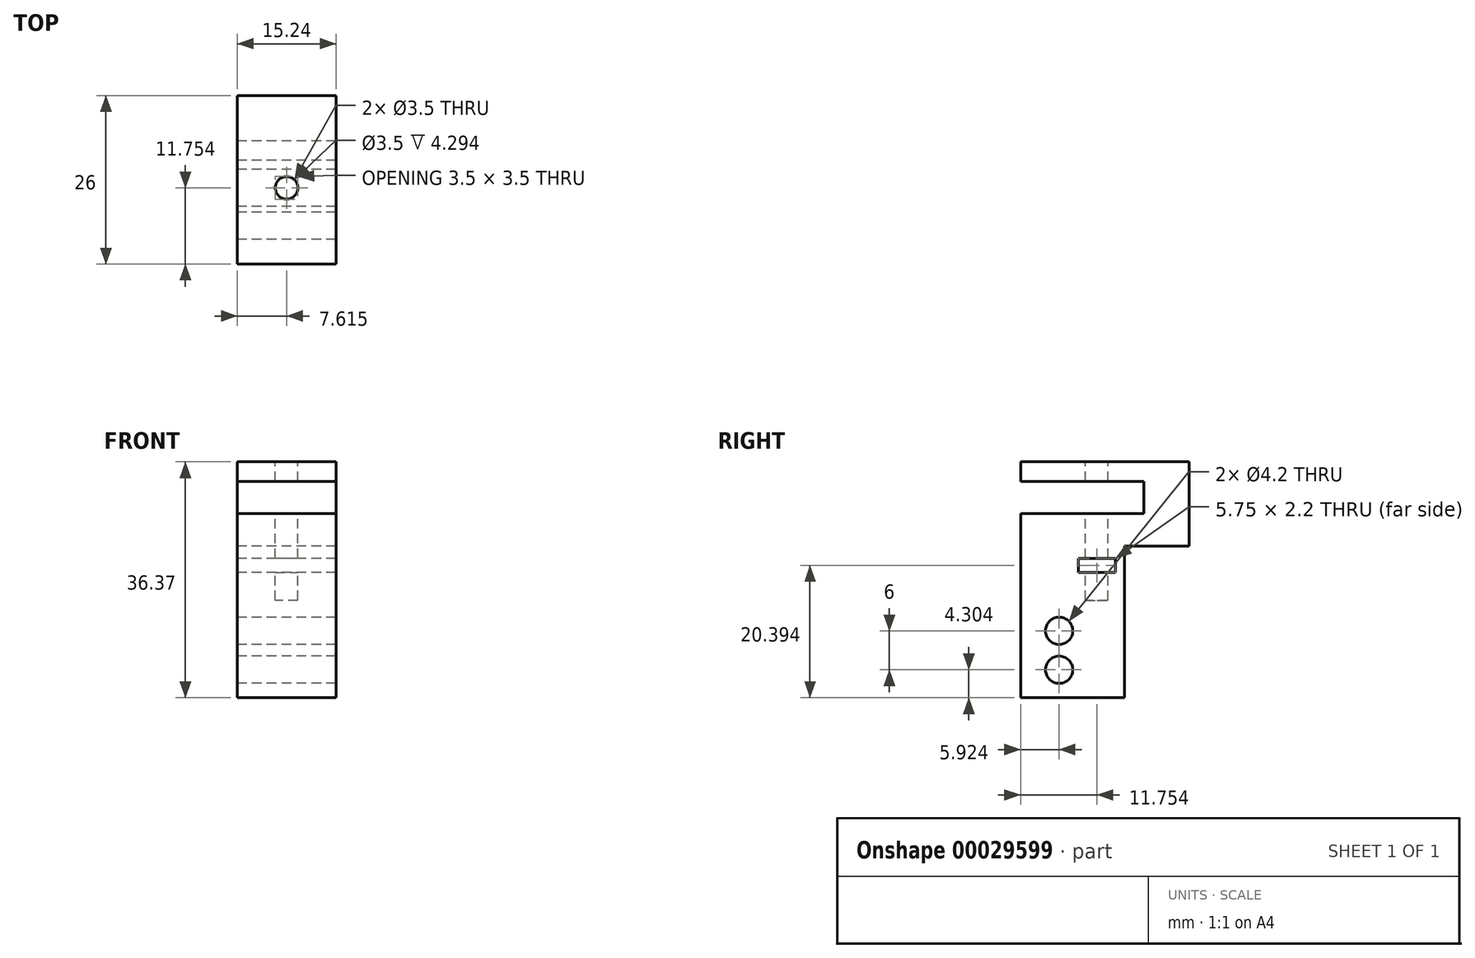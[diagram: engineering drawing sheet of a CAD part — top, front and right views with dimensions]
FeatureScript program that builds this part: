
annotation { "Feature Type Name" : "Feature", "Feature Type Description" : "" }
export const myFeature = defineFeature(function(context is Context, id is Id, definition is map)
    precondition{}
    {
        {
            var Q0;
            Q0=qCreatedBy(makeId("Top.planeOp"),FACE);
            var sketch = newSketch(context, id + "F0", { "sketchPlane" : qUnion([Q0])});
            skLineSegment(sketch, "E0.bottom", {"start": v(-10.08, 8.84) * mm, "end": v(5.16, 8.84) * mm});
            skLineSegment(sketch, "E0.top", {"start": v(-10.08, -9.16) * mm, "end": v(5.16, -9.16) * mm});
            skLineSegment(sketch, "E0.left", {"start": v(-10.08, 8.84) * mm, "end": v(-10.08, -9.16) * mm});
            skLineSegment(sketch, "E0.right", {"start": v(5.16, 8.84) * mm, "end": v(5.16, -9.16) * mm});
            skSolve(sketch);
        }
        {
            var Q0;
            Q0 = qSketchRegion(id + "F0", true);
            extrude(context, id + "F1", {"entities" : qUnion([Q0]), "depth" : 40 * mm});
        }
        {
            var Q0;
            Q0=makeQuery(id+"F1.opExtrude","SWEPT_FACE",FACE,{"disambiguationData":[OSD([sQuery(id+"F0.wireOp",EDGE,"E0.left")])]});
            var sketch = newSketch(context, id + "F2", { "sketchPlane" : qUnion([Q0])});
            skLineSegment(sketch, "E1.0", {"start": v(-8.84, 40) * mm, "end": v(9.16, 40) * mm, "construction": true});
            skLineSegment(sketch, "E2.0", {"start": v(9.16, 40) * mm, "end": v(9.16, 0) * mm, "construction": true});
            skLineSegment(sketch, "E3.0", {"start": v(-8.84, 40) * mm, "end": v(-8.84, 0) * mm, "construction": true});
            skLineSegment(sketch, "E4.0", {"start": v(-8.84, 0) * mm, "end": v(9.16, 0) * mm, "construction": true});
            skCircle(sketch, "E5", {"center": v(3.24, 10.3) * mm, "radius": 2.1 * mm});
            skLineSegment(sketch, "E6", {"start": v(3.24, 10.3) * mm, "end": v(3.24, -1.7) * mm, "construction": true});
            skCircle(sketch, "E7", {"center": v(3.24, 4.3) * mm, "radius": 2.1 * mm});
            skSolve(sketch);
        }
        {
            var Q0;
            Q0 = qSketchRegion(id + "F2", true);
            var Q1;
            Q1=makeQuery(id+"F1.opExtrude","SWEPT_FACE",FACE,{"disambiguationData":[OSD([sQuery(id+"F0.wireOp",EDGE,"E0.right")])]});
            extrude(context, id + "F3", {"entities" : qUnion([Q0]), "operationType" : NewBodyOperationType.REMOVE, "endBound" : BoundingType.UP_TO_SURFACE, "oppositeDirection" : true, "endBoundEntityFace" : qUnion([Q1]), "depth" : 25 * mm});
        }
        {
            var Q0;
            Q0=makeQuery(id+"F1.opExtrude","CAP_FACE",FACE,{"disambiguationData":[OSD([sQuery(id+"F0.wireOp",EDGE,"E0.bottom"),sQuery(id+"F0.wireOp",EDGE,"E0.top"),sQuery(id+"F0.wireOp",EDGE,"E0.left"),sQuery(id+"F0.wireOp",EDGE,"E0.right")])],"isStart":false});
            var sketch = newSketch(context, id + "F4", { "sketchPlane" : qUnion([Q0])});
            skLineSegment(sketch, "E8.0", {"start": v(-10.08, 8.84) * mm, "end": v(5.16, 8.84) * mm, "construction": true});
            skLineSegment(sketch, "E9", {"start": v(-2.46, 8.84) * mm, "end": v(-2.46, -17.2) * mm, "construction": true});
            skCircle(sketch, "E10", {"center": v(-2.46, 2.6) * mm, "radius": 1.75 * mm});
            skSolve(sketch);
        }
        {
            var Q0;
            Q0=makeQuery(id+"F4.imprint","IMPRINT",FACE,{"disambiguationData":[TD([[makeQuery(id+"F4.imprint","IMPRINT",EDGE,{"derivedFrom":sQuery(id+"F4.wireOp",EDGE,"E10")}),1.0]])]});
            extrude(context, id + "F5", {"entities" : qUnion([Q0]), "operationType" : NewBodyOperationType.REMOVE, "oppositeDirection" : true, "depth" : 25 * mm});
        }
        {
            var Q0;
            Q0=makeQuery(id+"F1.opExtrude","SWEPT_FACE",FACE,{"disambiguationData":[OSD([sQuery(id+"F0.wireOp",EDGE,"E0.left")])]});
            var sketch = newSketch(context, id + "F6", { "sketchPlane" : qUnion([Q0])});
            skLineSegment(sketch, "E11.0", {"start": v(-4.34, 25.3) * mm, "end": v(-0.84, 25.3) * mm, "construction": true});
            skLineSegment(sketch, "E12", {"start": v(-2.6, 25.3) * mm, "end": v(-2.6, 5.75) * mm, "construction": true});
            skLineSegment(sketch, "E13.bottom", {"start": v(-5.47, 21.5) * mm, "end": v(0.28, 21.5) * mm});
            skLineSegment(sketch, "E13.top", {"start": v(-5.47, 19.3) * mm, "end": v(0.28, 19.3) * mm});
            skLineSegment(sketch, "E13.left", {"start": v(-5.47, 21.5) * mm, "end": v(-5.47, 19.3) * mm});
            skLineSegment(sketch, "E13.right", {"start": v(0.28, 21.5) * mm, "end": v(0.28, 19.3) * mm});
            skLineSegment(sketch, "E14.0", {"start": v(-8.84, 40) * mm, "end": v(-8.84, 0) * mm, "construction": true});
            skSolve(sketch);
        }
        {
            var Q0;
            Q0 = qSketchRegion(id + "F6", true);
            var Q1;
            Q1=makeQuery(id+"F1.opExtrude","SWEPT_FACE",FACE,{"disambiguationData":[OSD([sQuery(id+"F0.wireOp",EDGE,"E0.right")])]});
            extrude(context, id + "F7", {"entities" : qUnion([Q0]), "operationType" : NewBodyOperationType.REMOVE, "endBound" : BoundingType.UP_TO_SURFACE, "oppositeDirection" : true, "endBoundEntityFace" : qUnion([Q1]), "depth" : 25 * mm});
        }
        {
            var Q0;
            Q0=makeQuery(id+"F1.opExtrude","SWEPT_FACE",FACE,{"disambiguationData":[OSD([sQuery(id+"F0.wireOp",EDGE,"E0.left")])]});
            var sketch = newSketch(context, id + "F8", { "sketchPlane" : qUnion([Q0])});
            skLineSegment(sketch, "E15.0", {"start": v(-5.47, 21.5) * mm, "end": v(0.28, 21.5) * mm, "construction": true});
            skPoint(sketch, "E16.orphan", {"position": v(-8.84, 0) * mm});
            skLineSegment(sketch, "E17.0", {"start": v(-8.84, 40) * mm, "end": v(-8.84, 23.37) * mm});
            skLineSegment(sketch, "E18", {"start": v(-8.84, 40) * mm, "end": v(-18.84, 40) * mm});
            skLineSegment(sketch, "E19", {"start": v(-18.84, 40) * mm, "end": v(-18.84, 23.37) * mm});
            skLineSegment(sketch, "E20", {"start": v(-18.84, 23.37) * mm, "end": v(-8.84, 23.37) * mm});
            skSolve(sketch);
        }
        {
            var Q0;
            Q0 = qSketchRegion(id + "F8", true);
            var Q1;
            Q1=makeQuery(id+"F1.opExtrude","SWEPT_FACE",FACE,{"disambiguationData":[OSD([sQuery(id+"F0.wireOp",EDGE,"E0.right")])]});
            extrude(context, id + "F9", {"entities" : qUnion([Q0]), "endBound" : BoundingType.UP_TO_SURFACE, "oppositeDirection" : true, "endBoundEntityFace" : qUnion([Q1]), "depth" : 18 * mm});
        }
        {
            var Q0;
            Q0=makeQuery(id+"F1.opExtrude","SWEPT_BODY",BODY,{"disambiguationData":[OSD([sQuery(id+"F0.wireOp",EDGE,"E0.bottom"),sQuery(id+"F0.wireOp",EDGE,"E0.top"),sQuery(id+"F0.wireOp",EDGE,"E0.left"),sQuery(id+"F0.wireOp",EDGE,"E0.right")])]});
            var Q1;
            Q1=makeQuery(id+"F9.opExtrude","SWEPT_BODY",BODY,{"disambiguationData":[OSD([sQuery(id+"F8.wireOp",EDGE,"E17.0"),sQuery(id+"F8.wireOp",EDGE,"E18"),sQuery(id+"F8.wireOp",EDGE,"E19"),sQuery(id+"F8.wireOp",EDGE,"E20")])]});
            booleanBodies(context, id + "F10", {"operationType" : BooleanOperationType.UNION, "tools" : qUnion([Q0, Q1])});
        }
        {
            var Q0;
            Q0=makeQuery(id+"F1.opExtrude","SWEPT_FACE",FACE,{"disambiguationData":[OSD([sQuery(id+"F0.wireOp",EDGE,"E0.left")])]});
            var sketch = newSketch(context, id + "F11", { "sketchPlane" : qUnion([Q0])});
            skLineSegment(sketch, "E21.0", {"start": v(9.16, 40) * mm, "end": v(9.16, 0) * mm});
            skLineSegment(sketch, "E22", {"start": v(9.16, 28.37) * mm, "end": v(-9.84, 28.37) * mm});
            skLineSegment(sketch, "E23", {"start": v(-9.84, 28.37) * mm, "end": v(-9.84, 33.37) * mm});
            skLineSegment(sketch, "E24", {"start": v(-9.84, 33.37) * mm, "end": v(9.16, 33.37) * mm});
            skSolve(sketch);
        }
        {
            var Q0;
            Q0 = qSketchRegion(id + "F11", true);
            extrude(context, id + "F12", {"entities" : qUnion([Q0]), "operationType" : NewBodyOperationType.REMOVE, "oppositeDirection" : true, "depth" : 25 * mm});
        }
        {
            var Q0;
            Q0=makeQuery(id+"F10.opBoolean","MERGE",FACE,{"derivedFrom":[makeQuery(id+"F1.opExtrude","SWEPT_FACE",FACE,{"disambiguationData":[OSD([sQuery(id+"F0.wireOp",EDGE,"E0.left")])]}),makeQuery(id+"F9.opExtrude","CAP_FACE",FACE,{"disambiguationData":[OSD([sQuery(id+"F8.wireOp",EDGE,"E17.0"),sQuery(id+"F8.wireOp",EDGE,"E18"),sQuery(id+"F8.wireOp",EDGE,"E19"),sQuery(id+"F8.wireOp",EDGE,"E20")])],"isStart":true})]});
            var sketch = newSketch(context, id + "F13", { "sketchPlane" : qUnion([Q0])});
            skLineSegment(sketch, "E25.0.2", {"start": v(-9.84, 33.37) * mm, "end": v(9.16, 33.37) * mm, "construction": true});
            skLineSegment(sketch, "E26", {"start": v(-18.84, 43.06) * mm, "end": v(9.16, 43.06) * mm});
            skLineSegment(sketch, "E27", {"start": v(-18.84, 36.37) * mm, "end": v(9.16, 36.37) * mm});
            skLineSegment(sketch, "E28", {"start": v(-18.84, 43.06) * mm, "end": v(-18.84, 36.37) * mm});
            skLineSegment(sketch, "E29", {"start": v(9.16, 43.06) * mm, "end": v(9.16, 36.37) * mm});
            skSolve(sketch);
        }
        {
            var Q0;
            Q0 = qSketchRegion(id + "F13", true);
            extrude(context, id + "F14", {"entities" : qUnion([Q0]), "operationType" : NewBodyOperationType.REMOVE, "oppositeDirection" : true, "depth" : 25 * mm});
        }
        {
            var Q0;
            Q0=makeQuery(id+"F10.opBoolean","MERGE",FACE,{"derivedFrom":[makeQuery(id+"F1.opExtrude","SWEPT_FACE",FACE,{"disambiguationData":[OSD([sQuery(id+"F0.wireOp",EDGE,"E0.left")])]}),makeQuery(id+"F9.opExtrude","CAP_FACE",FACE,{"disambiguationData":[OSD([sQuery(id+"F8.wireOp",EDGE,"E17.0"),sQuery(id+"F8.wireOp",EDGE,"E18"),sQuery(id+"F8.wireOp",EDGE,"E19"),sQuery(id+"F8.wireOp",EDGE,"E20")])],"isStart":true})]});
            var sketch = newSketch(context, id + "F15", { "sketchPlane" : qUnion([Q0])});
            skLineSegment(sketch, "E30.0", {"start": v(-18.84, 36.37) * mm, "end": v(-18.84, 23.37) * mm});
            skLineSegment(sketch, "E31.0", {"start": v(-8.84, 23.37) * mm, "end": v(-8.84, 0) * mm});
            skLineSegment(sketch, "E32.0", {"start": v(-16.84, 36.37) * mm, "end": v(-16.84, 23.37) * mm});
            skLineSegment(sketch, "E33.0", {"start": v(-6.84, 23.37) * mm, "end": v(-6.84, 0) * mm});
            skLineSegment(sketch, "E34", {"start": v(-18.84, 36.37) * mm, "end": v(-16.84, 36.37) * mm});
            skLineSegment(sketch, "E35", {"start": v(-18.84, 23.37) * mm, "end": v(-16.84, 23.37) * mm});
            skLineSegment(sketch, "E36", {"start": v(-8.84, 23.37) * mm, "end": v(-6.84, 23.37) * mm});
            skLineSegment(sketch, "E37", {"start": v(-8.84, 0) * mm, "end": v(-6.84, 0) * mm});
            skSolve(sketch);
        }
        {
            var Q0;
            Q0 = qSketchRegion(id + "F15", true);
            var Q1;
            Q1=makeQuery(id+"F10.opBoolean","MERGE",FACE,{"derivedFrom":[makeQuery(id+"F1.opExtrude","SWEPT_FACE",FACE,{"disambiguationData":[OSD([sQuery(id+"F0.wireOp",EDGE,"E0.right")])]}),makeQuery(id+"F9.opExtrude","CAP_FACE",FACE,{"disambiguationData":[OSD([sQuery(id+"F8.wireOp",EDGE,"E17.0"),sQuery(id+"F8.wireOp",EDGE,"E18"),sQuery(id+"F8.wireOp",EDGE,"E19"),sQuery(id+"F8.wireOp",EDGE,"E20")])],"isStart":false})]});
            extrude(context, id + "F16", {"entities" : qUnion([Q0]), "operationType" : NewBodyOperationType.REMOVE, "endBound" : BoundingType.UP_TO_SURFACE, "oppositeDirection" : true, "endBoundEntityFace" : qUnion([Q1]), "depth" : 25 * mm});
        }
    });
